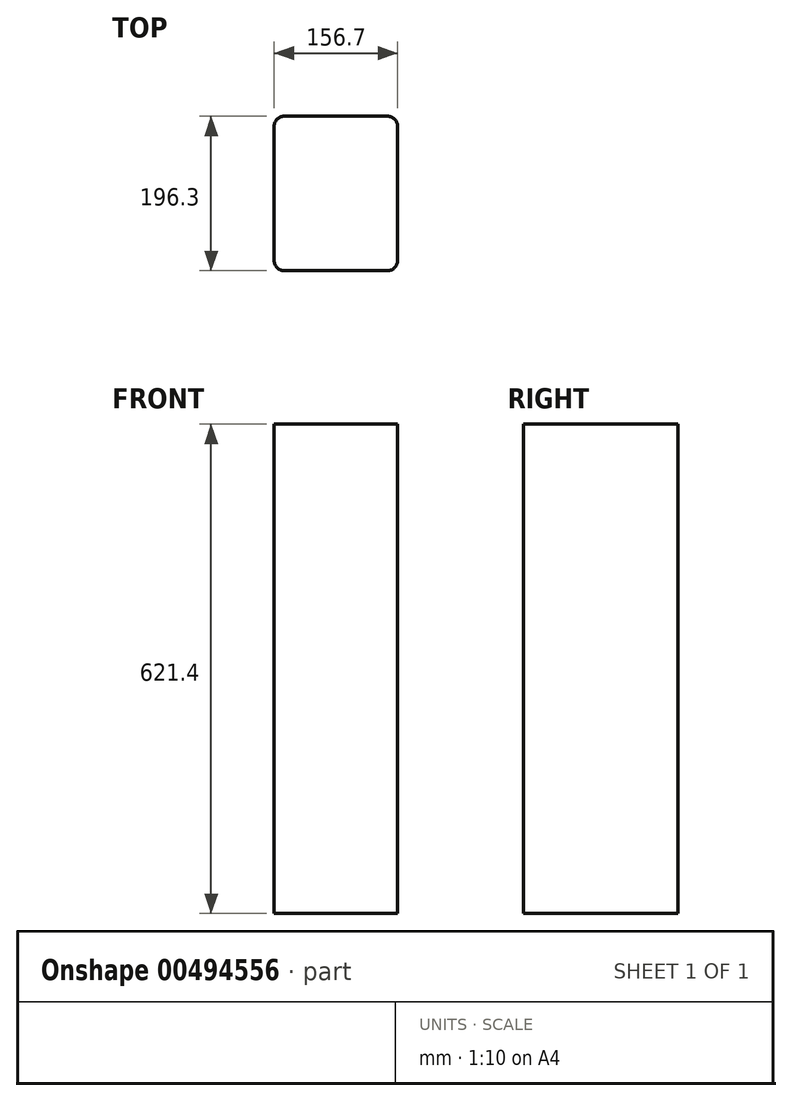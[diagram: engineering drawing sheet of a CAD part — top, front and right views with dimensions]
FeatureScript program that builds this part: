
annotation { "Feature Type Name" : "Feature", "Feature Type Description" : "" }
export const myFeature = defineFeature(function(context is Context, id is Id, definition is map)
    precondition{}
    {
        {
            var Q0;
            Q0=qCreatedBy(makeId("Front.planeOp"),FACE);
            var sketch = newSketch(context, id + "F0", { "sketchPlane" : qUnion([Q0])});
            skLineSegment(sketch, "E0.bottom", {"start": v(0, 0) * mm, "end": v(-156.7, 0) * mm});
            skLineSegment(sketch, "E0.top", {"start": v(0, 621.4) * mm, "end": v(-156.7, 621.4) * mm});
            skLineSegment(sketch, "E0.left", {"start": v(0, 0) * mm, "end": v(0, 621.4) * mm});
            skLineSegment(sketch, "E0.right", {"start": v(-156.7, 0) * mm, "end": v(-156.7, 621.4) * mm});
            skSolve(sketch);
        }
        {
            var Q0;
            Q0=qSketchRegion(id+"F0",true);
            extrude(context, id + "F1", {"entities" : qUnion([Q0]), "depth" : 196.3 * mm});
        }
        {
            var Q0;
            Q0=makeQuery(id+"F1.opExtrude","CAP_EDGE",EDGE,{"disambiguationData":[OSD([sQuery(id+"F0.wireOp",EDGE,"E0.right")])],"isStart":true});
            var Q1;
            Q1=makeQuery(id+"F1.opExtrude","CAP_EDGE",EDGE,{"disambiguationData":[OSD([sQuery(id+"F0.wireOp",EDGE,"E0.right")])],"isStart":false});
            var Q2;
            Q2=makeQuery(id+"F1.opExtrude","CAP_EDGE",EDGE,{"disambiguationData":[OSD([sQuery(id+"F0.wireOp",EDGE,"E0.left")])],"isStart":false});
            var Q3;
            Q3=makeQuery(id+"F1.opExtrude","CAP_EDGE",EDGE,{"disambiguationData":[OSD([sQuery(id+"F0.wireOp",EDGE,"E0.left")])],"isStart":true});
            fillet(context, id + "F2", {"entities" : qUnion([Q0, Q1, Q2, Q3]), "radius" : 12.7 * mm, "tangentPropagation" : true, "allowEdgeOverflow" : false});
        }
    });
